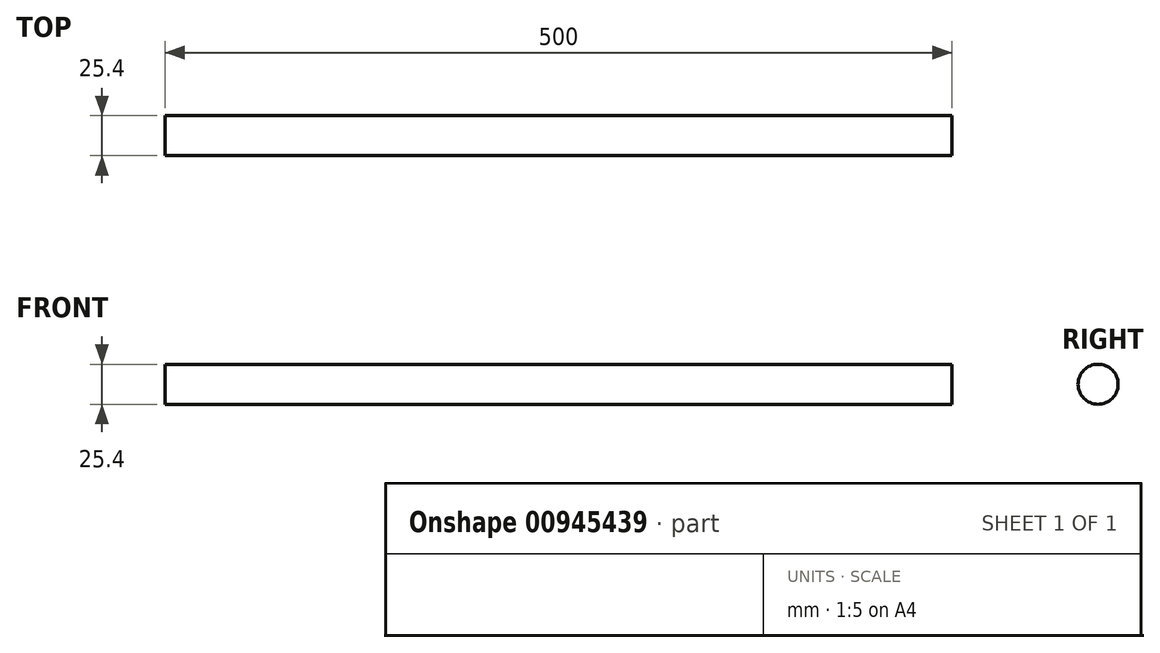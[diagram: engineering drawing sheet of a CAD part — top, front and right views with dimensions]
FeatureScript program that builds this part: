
annotation { "Feature Type Name" : "Feature", "Feature Type Description" : "" }
export const myFeature = defineFeature(function(context is Context, id is Id, definition is map)
    precondition{}
    {
        {
            var Q0;
            Q0=qCreatedBy(makeId("Right.planeOp"),FACE);
            var sketch = newSketch(context, id + "F0", { "sketchPlane" : qUnion([Q0])});
            skCircle(sketch, "E0", {"center": v(0, 0) * mm, "radius": 12.7 * mm});
            skSolve(sketch);
        }
        {
            var Q0;
            Q0=sQuery(id+"F0.wireOp",EDGE,"E0");
            extrude(context, id + "F1", {"bodyType" : ToolBodyType.SURFACE, "surfaceEntities" : qUnion([Q0]), "depth" : 500 * mm, "offsetDistance" : 25.4 * mm});
        }
    });
